# Revit family: HVAC_Water-Heaters_Enertech_CTC_Modul-300-E15
name_source: partatom
category: Specialty Equipment
revit_build: Autodesk Revit 2018 (Build: 20170223_1515(x64)
units: mm (PartAtom-declared; Revit-internal decimal feet)

## family parameters
Always vertical = No
Cut with Voids When Loaded = No
OmniClass Number = 23.75.00.00
OmniClass Title = Climate Control (HVAC)
Part Type = Normal
Room Calculation Point = No
Round Connector Dimension = Use Diameter
Shared = No
Work Plane-Based = No

## types (1)
- CTC Modul 300 E15
    AssetType = Fixed
    BIMObjectName = HVAC_Water-Heaters_Enertech_CTC_Modul-300-E15
    Brand = CTC
    Category = Water heater
    Color = white
    Cost = 0 $
    Description = A stainless steel hot water heater, specially developed for high hot water demands, suitable for use together with heat pumps, solar panels or other external heat sources. 
The series comprises of heaters and a tank, which can be easily connected in series to the capacity of your choice.
    DurationUnit = Year
    EANNumber = 7333077095468
    ElectricalDeviceNominalPower = 15000 W
    EnergyClass_HotWater = D / XL
    EnergyClass_HotWater_TapProfile = A/XL
    GroupFuse = 13 A / 25 A
    HasProtectiveEarth = Yes
    HotTapWaterPerformance = 429.9 liters
    IP_Code = IP44
    IfcExportAs = IfcElectricalDeviceCommon
    IfcExportType = HEATER
    Manufacturer = Enertech AB
    ManufacturerCountry = Sweden
    ManufacturerName = Enertech AB
    ManufacturerURL = https://ctc.se
    Material = Steel
    MaxOperatingPressureHotWater = 10 bar
    MinimumCeilingHeight = 1660 mm
    Model = CTC Modul 300 E15
    ModelNumber = 589800001
    NBSDescription = Air to water heat pumps
    NBSReference = 90-40-40/320
    Name = CTC_Modul-300-E15
    NominalCurrent = 0 A
    NominalDepth = 585 mm
    NominalFrequencyRange = 60 Hz
    NominalHeight = 1594 mm
    NominalVoltage = 400 V
    NominalWidth = 585 mm
    NumberOfPoles = 3
    OutputRangeIimmersionHeater = 2.5 - 7.5 kW / 5 - 15 kW
    PhaseAngle = 0.00°
    PowerFactor = 0 W
    ProductInformation = A stainless steel hot water heater, specially developed for high hot water demands, suitable for use together with heat pumps, solar panels or other external heat sources. 
The series comprises of heaters and a tank, which can be easily connected in series to the capacity of your choice.
    PumpMainMaterial = Stainless Steel
    PumpSecondaryMaterial = Brass
    RatedCurrent = 22 A
    RatedVoltage = 1200 V
    Shape = round
    Size = Ø 585 x 1582 mm
    SoundPowerLWA = 15 dB(A)
    Touchscreen = no
    UNSPSCCode = 40101825
    URL = https://ctc.se
    Uniclass2 = Pr_40_70_65
    Uniclass2015Description = Preparation catering equipment
    Uniclass2015Reference = Pr_40_70_65
    UsageCurrent = 0 A
    Version = 1
    VersionDate = 24/05/2022
    WarrantyDurationUnit = Year
    WaterVolumeWaterSuply = 282 liters
    Weight = 49 kg

## geometry (parser evidence)
native form markers: Sweep x5
no freeform markers — native parametric forms only
